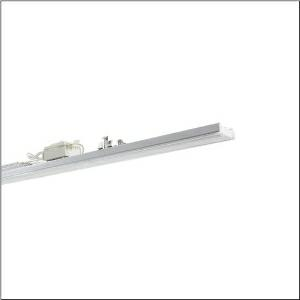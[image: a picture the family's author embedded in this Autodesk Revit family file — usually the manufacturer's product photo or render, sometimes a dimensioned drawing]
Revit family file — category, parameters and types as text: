
# Revit family: licross_21_recessed_mo_52tl127n455g
name_source: partatom
category: Lighting Fixtures
units: mm (PartAtom-declared; Revit-internal decimal feet)

## family parameters
Cut with Voids When Loaded = No
Host = Face
Light Source = No
Part Type = Normal
Room Calculation Point = No
Round Connector Dimension = Use Diameter
Shared = No

## types (1)
- Licross 21 Recessed MO (1 x LED, 5600 lm, 29.8 W, 4000K)
    Apparent Load = 30 VA
    CIE Flux Codes = 72 92 99 100 100
    Color Rendering = 80
    Color Temperature = 4000K
    Default Elevation = 1800 mm
    Description = Licross 21 Recessed MO, luminaire insert, of sheet steel, galvanised, coil coated, white, length: 1.500mm, width: 66mm, height: 67mm, LED rated luminous flux: 5.600lm, light colour: 840, SDCM (Standard Deviation of Colour Matching)MacAdam ≤ 3 SDCM (initial), control gear: ON/OFF, with plug, 3-pole, with phase selection, mains connection: 220..240V, AC, 50/60Hz, rated input power: 30W, internal wiring halogen-free, primary optical cover: cover, of PMMA, light emission: direct distribution, primary light characteristic: symmetric, protection rating (complete): IP40, insulation class (complete): insulation class I (protective earthing), certification: CE, ENEC, VDE, UKCA, protection symbol: D if used in an environment without relevant dust loads with corresponding accessories, impact resistance: IK06, permissible ambient temperature for indoor applications: -35..+50°C, corresponds to IFS (International Featured Standards) requirements for safety and quality in the food industry, reducing of maximum allowable ambient temperature of 5°C with ceiling mounting, LABS conformity tested according to VDMA 24364:2018-05, The light source and the operating device comply with the requirements of the Ecodesign Regulation (EU) 2019/2020 and are replaceable in accordance with this regulation, packaging unit: 1 piece
    Height = 58 mm
    Lamp = 1 x LED
    Lamp Light Flux = 5600 lm
    Lamp Power = 29.8 W
    Lamp count = 1
    Length = 1500 mm
    Luminous efficacy = 188 lm/W
    Manufacturer = Siteco
    ModVariant = No
    Model = 52TL127N455G
    Mounting Place = Ceiling
    Mounting Type = Pendant
    Number of Poles = 1
    OnlyDefault = Yes
    Power Factor = 1
    Product Name = Licross 21 Recessed MO
    Product group = luminaire insert | ceiling pendant
    ProductGroupID = 901
    Protection Class = Protection class I
    Protection Degree = IP 40
    RLX_Detail_Level = 1
    RLX_Emergency_Light_Flux = 0 lm
    RLX_Emergency_Type = 0
    RLX_Emergency_Type_DB = No
    RlxData = <blob elided: 21197 chars, md5=c35fc741>
    Socket = socket
    Standby Power = 0 W
    System Light Flux = 5600 lm
    System Power = 30 W
    Type Comments = Product without accessories
    Type Image = l_1296930.jpg
    URL = http://relux.com
    VarID = ---
    Voltage = 0 V
    Weight = 0.00 kg
    Width = 66 mm

## geometry (parser evidence)
native form markers: Blend x4, Sweep x11
no freeform markers — native parametric forms only
